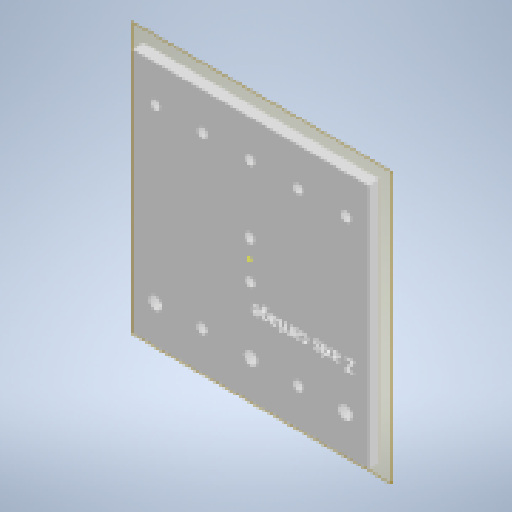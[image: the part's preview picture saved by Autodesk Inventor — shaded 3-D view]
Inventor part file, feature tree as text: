
AUTODESK INVENTOR PART (.ipt)
format: ipt  version: 2023.2 (Build 272271000, 271)  size: 184,832 bytes
history: native  units: mm
features: reference x8, sketch x5, hole x3, other x3, plane x1, extrude x1
ambient origin geometry x8: Origin, YZ Plane, XZ Plane, XY Plane, X Axis, Y Axis, Z Axis, Center Point
bodies: Solid1 (feature_tree)
feature tree (21):
  plane  "Work Plane1"
  extrude  "Extrusion1"  Depth=50.2mm
  hole  "Hole1"  [1 undecoded]
  hole  "Hole2"  [1 undecoded]
  hole  "Hole3"  [1 undecoded]
  sketch  "Sketch5"  dims[d8=7.1mm d9=6.0mm d10=7.5mm d11=2.0mm d12=90.0deg d13=8.0mm d14=20.594885mm d15=5.1mm d16=6.0mm d17=7.5mm d18=2.0mm d19=90.0deg d20=8.0mm d21=20.594885mm d22=5.1mm d23=6.0mm d24=7.5mm d25=2.0mm d26=90.0deg d27=8.0mm d28=20.594885mm]
  sketch  "Sketch1"  dims[d0=100.4mm d1=50.2mm]
  reference  "Reference1"
  reference  "Reference2"
  reference  "Reference3"
  reference  "Reference4"
  reference  "Reference5"
  reference  "Reference6"
  reference  "Reference7"
  reference  "Reference8"
  sketch  "Sketch2"  dims[d2=25.1mm d3=25.1mm]
  sketch  "Sketch3"  dims[d4=10.0mm d5=20.0mm]
  sketch  "Sketch4"  dims[d6=6.0mm d7=0.0mm]
  parser-record x1  (decoder bookkeeping rows leaked as tree rows — omitted from the tree; the rows remain in map.json)
  other  "Main Assembly.iam"
  other  "X axis carriage small:1"
note: 3 required parameter values undecoded (feature->parameter linkage not recoverable at this tier; creation-order binding heuristic only, values carry confidence <= 0.55)
note: 1 file-system path scrubbed to <path> (originals preserved in map.json)
